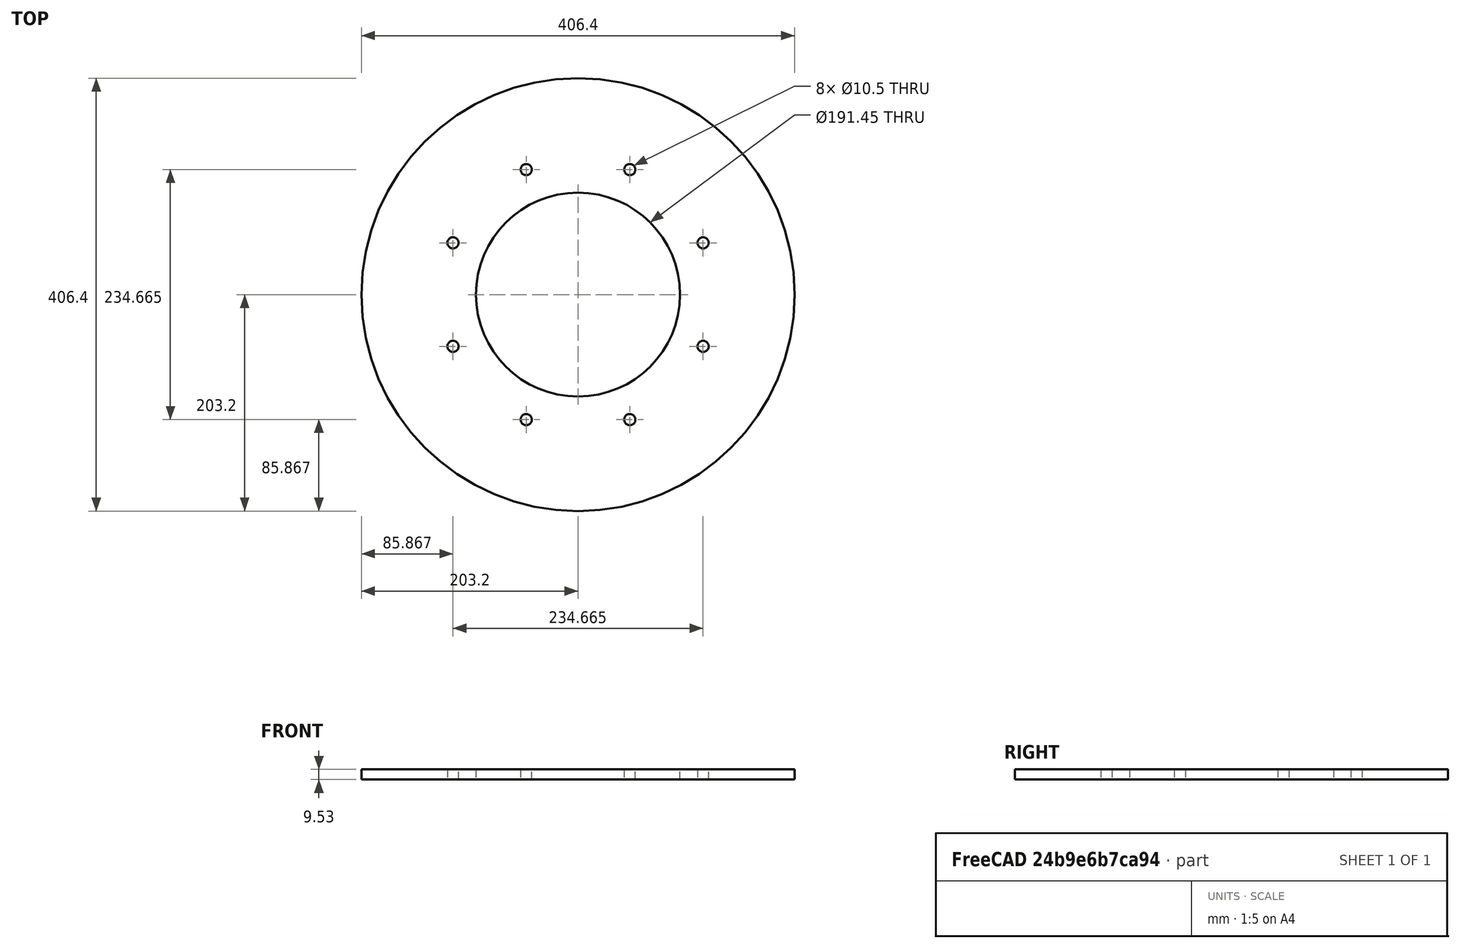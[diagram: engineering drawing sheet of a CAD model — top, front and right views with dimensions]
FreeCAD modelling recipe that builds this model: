
FCSTD DOCUMENT  (FreeCAD 0.21R33771 (Git))
Label: UQM_FACEPLATE_20240629_1
License: All rights reserved
LicenseURL: http://en.wikipedia.org/wiki/All_rights_reserved
objects: PartDesign::Plane×2, Sketcher::SketchObject×1, PartDesign::Pad×1, PartDesign::Line×1, PartDesign::Body×1
note: 7 computed .brp shape members not serialized (recipe doc carries the construction recipe); baked Part::Feature solids carry a one-line shape summary decoded from their .brp

FEATURE [Sketcher::SketchObject] Sketch
  FullyConstrained = true
  MapMode = 5
  Support = -> [XY_Plane]
  expr: Constraints[11] = 180 - 22.5
  expr: Constraints[13] = 16 in
  expr: Constraints[3] = 7.4982 in + 1 mm
  sketch-geometry (19):
    g0: Circle CenterX=0 CenterY=0 CenterZ=0 NormalX=0 NormalY=0 NormalZ=1 AngleXU=0 Radius=127
    g1: Circle CenterX=0 CenterY=0 CenterZ=0 NormalX=0 NormalY=0 NormalZ=1 AngleXU=0 Radius=95.7271
    g2: Circle CenterX=-117.333 CenterY=48.6008 CenterZ=0 NormalX=0 NormalY=0 NormalZ=1 AngleXU=0 Radius=5.25
    g3: LineSegment StartX=0 StartY=0 StartZ=0 EndX=-117.333 EndY=48.6008 EndZ=0
    g4: LineSegment StartX=-117.333 StartY=48.6008 StartZ=0 EndX=-117.333 EndY=0 EndZ=0
    g5: Circle CenterX=0 CenterY=0 CenterZ=0 NormalX=0 NormalY=0 NormalZ=1 AngleXU=0 Radius=203.2
    g6: Circle CenterX=-117.333 CenterY=-48.6008 CenterZ=0 NormalX=0 NormalY=0 NormalZ=1 AngleXU=0 Radius=5.25
    g7: Circle CenterX=-48.6008 CenterY=-117.333 CenterZ=0 NormalX=0 NormalY=0 NormalZ=1 AngleXU=0 Radius=5.25
    g8: Circle CenterX=-48.6008 CenterY=117.333 CenterZ=0 NormalX=0 NormalY=0 NormalZ=1 AngleXU=0 Radius=5.25
    g9: Circle CenterX=48.6008 CenterY=117.333 CenterZ=0 NormalX=0 NormalY=0 NormalZ=1 AngleXU=0 Radius=5.25
    g10: Circle CenterX=117.333 CenterY=48.6008 CenterZ=0 NormalX=0 NormalY=0 NormalZ=1 AngleXU=0 Radius=5.25
    g11: Circle CenterX=48.6008 CenterY=-117.333 CenterZ=0 NormalX=0 NormalY=0 NormalZ=1 AngleXU=0 Radius=5.25
    g12: Circle CenterX=117.333 CenterY=-48.6008 CenterZ=0 NormalX=0 NormalY=0 NormalZ=1 AngleXU=0 Radius=5.25
    g13: LineSegment StartX=-117.333 StartY=0 StartZ=0 EndX=-117.333 EndY=-48.6008 EndZ=0
    g14: LineSegment StartX=-117.333 StartY=48.6008 StartZ=0 EndX=117.333 EndY=48.6008 EndZ=0
    g15: LineSegment StartX=-117.333 StartY=-48.6008 StartZ=0 EndX=117.333 EndY=-48.6008 EndZ=0
    g16: LineSegment StartX=117.333 StartY=48.6008 StartZ=0 EndX=117.333 EndY=-48.6008 EndZ=0
    g17: LineSegment StartX=-48.6008 StartY=117.333 StartZ=0 EndX=48.6008 EndY=117.333 EndZ=0
    g18: LineSegment StartX=-48.6008 StartY=-117.333 StartZ=0 EndX=48.6008 EndY=-117.333 EndZ=0
  constraints (49):
    c: Coincident(g0,g-1)
    c: Diameter(g0) = 254
    c: Coincident(g1,g0)
    c: Diameter(g1) = 191.454
    c: Diameter(g2) = 10.5
    c: PointOnObject(g2,g0)
    c: Coincident(g3,g1)
    c: Coincident(g3,g2)
    c: Coincident(g4,g2)
    c: PointOnObject(g4,g-1)
    c: Vertical(g4)
    c: Angle(g-1,g3) = 2.74889
    c: Coincident(g5,g1)
    c: Diameter(g5) = 406.4
    c: PointOnObject(g6,g0)
    c: PointOnObject(g7,g0)
    c: PointOnObject(g8,g0)
    c: PointOnObject(g9,g0)
    c: PointOnObject(g10,g0)
    c: PointOnObject(g11,g0)
    c: PointOnObject(g12,g0)
    c: Equal(g2,g8)
    c: Equal(g2,g9)
    c: Equal(g2,g10)
    c: Equal(g2,g6)
    c: Equal(g2,g7)
    c: Equal(g2,g11)
    c: Equal(g2,g12)
    c: Coincident(g13,g4)
    c: Coincident(g13,g6)
    c: Vertical(g13)
    c: Coincident(g14,g2)
    c: Coincident(g14,g10)
    c: Horizontal(g14)
    c: Coincident(g15,g6)
    c: Coincident(g15,g12)
    c: Horizontal(g15)
    c: Coincident(g16,g10)
    c: Coincident(g16,g12)
    c: Coincident(g17,g8)
    c: Coincident(g17,g9)
    c: Horizontal(g17)
    c: Equal(g16,g17)
    c: Coincident(g18,g7)
    c: Coincident(g18,g11)
    c: Horizontal(g18)
    c: Equal(g16,g18)
    c: DistanceY(g7,g8) = 234.665
    c: DistanceX(g2,g10) = 234.665
FEATURE [PartDesign::Pad] Pad
  Direction = (0,0,1)
  Length = 9.525
  Length2 = 10
  Profile = -> Sketch
  ReferenceAxis = -> Sketch [N_Axis]
  Type = 0
  expr: Length = 0.375 in
FEATURE [PartDesign::Plane] Plane_1
  Length = 100
  ResizeMode = 1
  Support = -> [XY_Plane]
  Width = 100
FEATURE [PartDesign::Line] Axis_1
  AttacherType = Attacher::AttachEngineLine
  Length = 200
  ResizeMode = 1
  Support = -> [Z_Axis]
FEATURE [PartDesign::Plane] Plane_2
  Length = 100
  ResizeMode = 1
  Support = -> [YZ_Plane]
  Width = 100
FEATURE [PartDesign::Body] Body
  Group = -> [Sketch,Pad,Plane_1,Axis_1,Plane_2]
  Origin = -> Origin
  Tip = -> Pad
